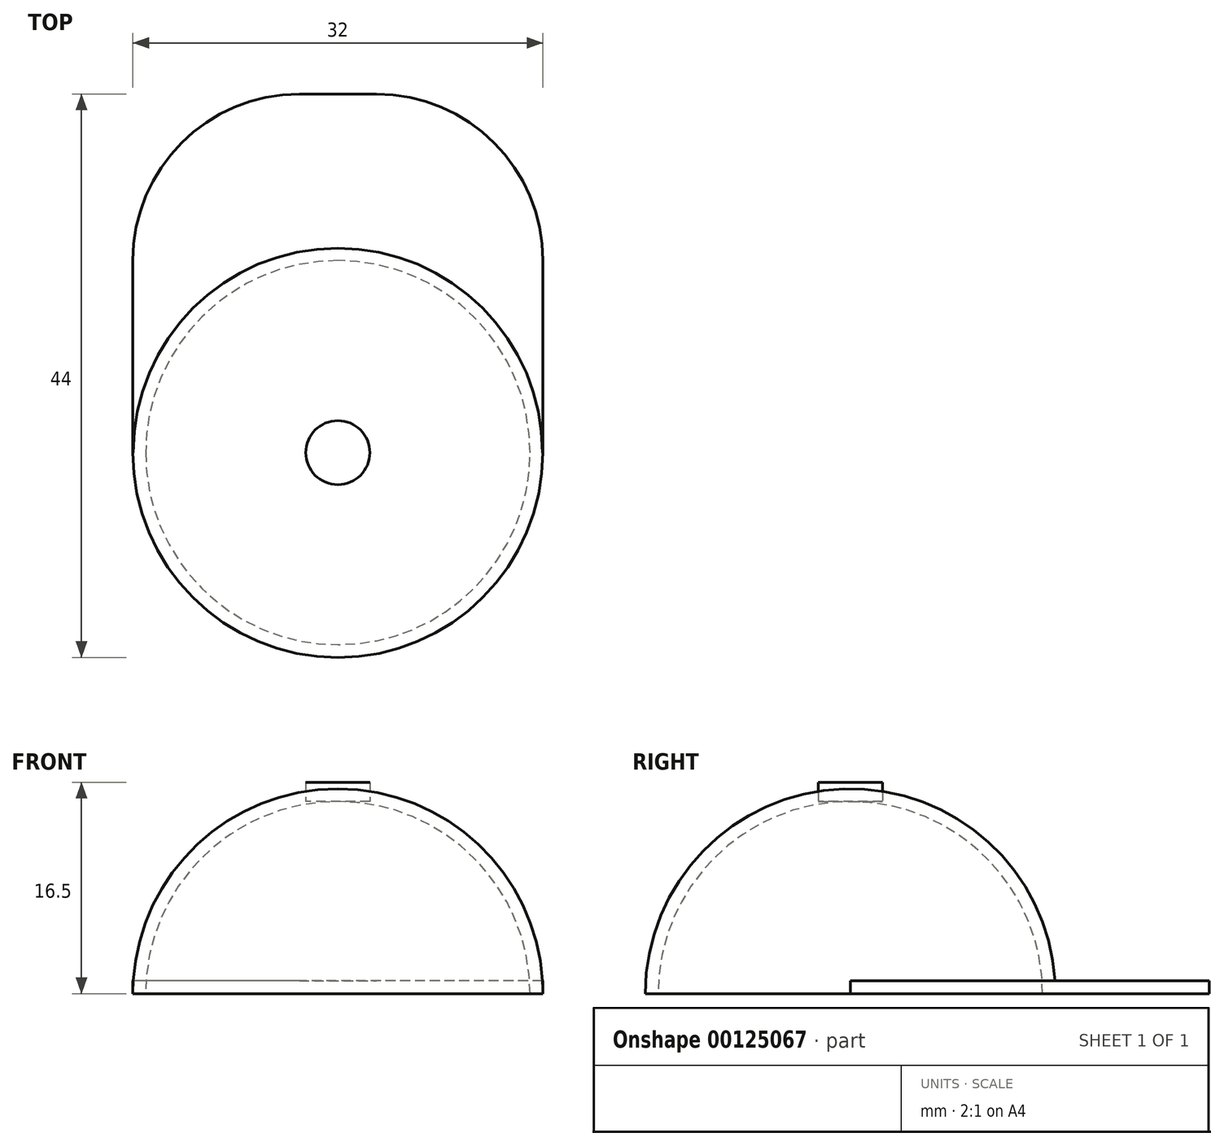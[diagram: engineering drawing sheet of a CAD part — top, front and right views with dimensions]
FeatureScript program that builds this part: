
annotation { "Feature Type Name" : "Feature", "Feature Type Description" : "" }
export const myFeature = defineFeature(function(context is Context, id is Id, definition is map)
    precondition{}
    {
        {
            var Q0;
            Q0=qCreatedBy(makeId("Front.planeOp"),FACE);
            var sketch = newSketch(context, id + "F0", { "sketchPlane" : qUnion([Q0])});
            skLineSegment(sketch, "E0", {"start": v(-16, 0) * mm, "end": v(16, 0) * mm});
            skArc(sketch, "E1", {"start": v(16, 0) * mm, "mid": v(0, 16) * mm, "end": v(-16, 0) * mm});
            skSolve(sketch);
        }
        {
            var Q0;
            Q0=qCreatedBy(makeId("Front.planeOp"),FACE);
            var sketch = newSketch(context, id + "F1", { "sketchPlane" : qUnion([Q0])});
            skLineSegment(sketch, "E2", {"start": v(-37.74, 0) * mm, "end": v(43.87, 0) * mm});
            skSolve(sketch);
        }
        {
            var Q0;
            Q0=makeQuery(id+"F0.imprint","IMPRINT",FACE,{"disambiguationData":[TD([[makeQuery(id+"F0.imprint","IMPRINT",EDGE,{"derivedFrom":sQuery(id+"F0.wireOp",EDGE,"E0")}),1.0]])]});
            var Q1;
            Q1=sQuery(id+"F1.wireOp",EDGE,"E2");
            revolve(context, id + "F2", {"entities" : qUnion([Q0]), "axis" : qUnion([Q1]), "revolveType" : RevolveType.SYMMETRIC, "angle" : 180 * degree});
        }
        {
            var Q0;
            Q0=qCreatedBy(makeId("Top.planeOp"),FACE);
            var sketch = newSketch(context, id + "F3", { "sketchPlane" : qUnion([Q0])});
            skLineSegment(sketch, "E3.bottom", {"start": v(-16, 0) * mm, "end": v(16, 0) * mm});
            skLineSegment(sketch, "E3.top", {"start": v(-3, 28) * mm, "end": v(3, 28) * mm});
            skLineSegment(sketch, "E3.left", {"start": v(-16, 0) * mm, "end": v(-16, 15) * mm});
            skLineSegment(sketch, "E3.right", {"start": v(16, 0) * mm, "end": v(16, 15) * mm});
            skPoint(sketch, "E4.visualSharp", {"position": v(16, 28) * mm});
            skArc(sketch, "E4.filletArc", {"start": v(16, 15) * mm, "mid": v(12.2, 24.2) * mm, "end": v(3, 28) * mm});
            skPoint(sketch, "E5.visualSharp", {"position": v(-16, 28) * mm});
            skArc(sketch, "E5.filletArc", {"start": v(-3, 28) * mm, "mid": v(-12.2, 24.2) * mm, "end": v(-16, 15) * mm});
            skSolve(sketch);
        }
        {
            var Q0;
            Q0 = qSketchRegion(id + "F3", true);
            extrude(context, id + "F4", {"entities" : qUnion([Q0]), "operationType" : NewBodyOperationType.ADD, "depth" : 1 * mm});
        }
        {
            var Q0;
            Q0=makeQuery(id+"F4.boolean.opBoolean","MERGE",FACE,{"derivedFrom":[makeQuery(id+"F2.opRevolve","CAP_FACE",FACE,{"disambiguationData":[OSD([sQuery(id+"F0.wireOp",EDGE,"E0"),sQuery(id+"F0.wireOp",EDGE,"E1")])],"isStart":true}),makeQuery(id+"F4.opExtrude","CAP_FACE",FACE,{"disambiguationData":[OSD([sQuery(id+"F3.wireOp",EDGE,"E3.bottom"),sQuery(id+"F3.wireOp",EDGE,"E3.top"),sQuery(id+"F3.wireOp",EDGE,"E3.left"),sQuery(id+"F3.wireOp",EDGE,"E3.right"),sQuery(id+"F3.wireOp",EDGE,"E4.filletArc"),sQuery(id+"F3.wireOp",EDGE,"E5.filletArc")])],"isStart":true})]});
            shell(context, id + "F5", {"entities" : qUnion([Q0]), "thickness" : 1 * mm});
        }
        {
            var Q0;
            Q0=qCreatedBy(makeId("Top.planeOp"),FACE);
            cPlane(context, id + "F6", {"entities" : qUnion([Q0]), "cplaneType" : CPlaneType.OFFSET, "offset" : 15 * mm, "width" : 150 * mm, "height" : 150 * mm});
        }
        {
            var Q0;
            Q0=qCreatedBy(id+"F6.planeOp",FACE);
            var sketch = newSketch(context, id + "F7", { "sketchPlane" : qUnion([Q0])});
            skCircle(sketch, "E6", {"center": v(0, 0) * mm, "radius": 2.5 * mm});
            skSolve(sketch);
        }
        {
            var Q0;
            Q0 = qSketchRegion(id + "F7", true);
            extrude(context, id + "F8", {"entities" : qUnion([Q0]), "depth" : 1.5 * mm});
        }
    });
